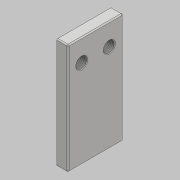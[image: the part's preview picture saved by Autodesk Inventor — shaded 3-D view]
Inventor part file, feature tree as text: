
AUTODESK INVENTOR PART (.ipt)
format: ipt  version: 2018 (Build 220112000, 112)  size: 112,640 bytes
history: native  units: mm
features: other x3, chamfer x2, sketch x2, extrude x1, fillet x1, hole x1
ambient origin geometry x8: Origin, YZ Plane, XZ Plane, XY Plane, X Axis, Y Axis, Z Axis, Center Point
bodies: Body1 (feature_tree)
feature tree (10):
  other  "實體1"
  extrude  "擠出1"  Depth=50.0mm
  fillet  "圓角1"  Radius=100.0mm
  chamfer  "倒角1"  Distance=10.0mm
  hole  "孔1"  [1 undecoded]
  other  "螺紋1"
  other  "螺紋2"
  chamfer  "倒角2"  Distance=1.0mm Angle=45.0deg
  sketch  "草圖1"
  sketch  "草圖2"
note: 1 required parameter value undecoded (feature->parameter linkage not recoverable at this tier; creation-order binding heuristic only, values carry confidence <= 0.55)
